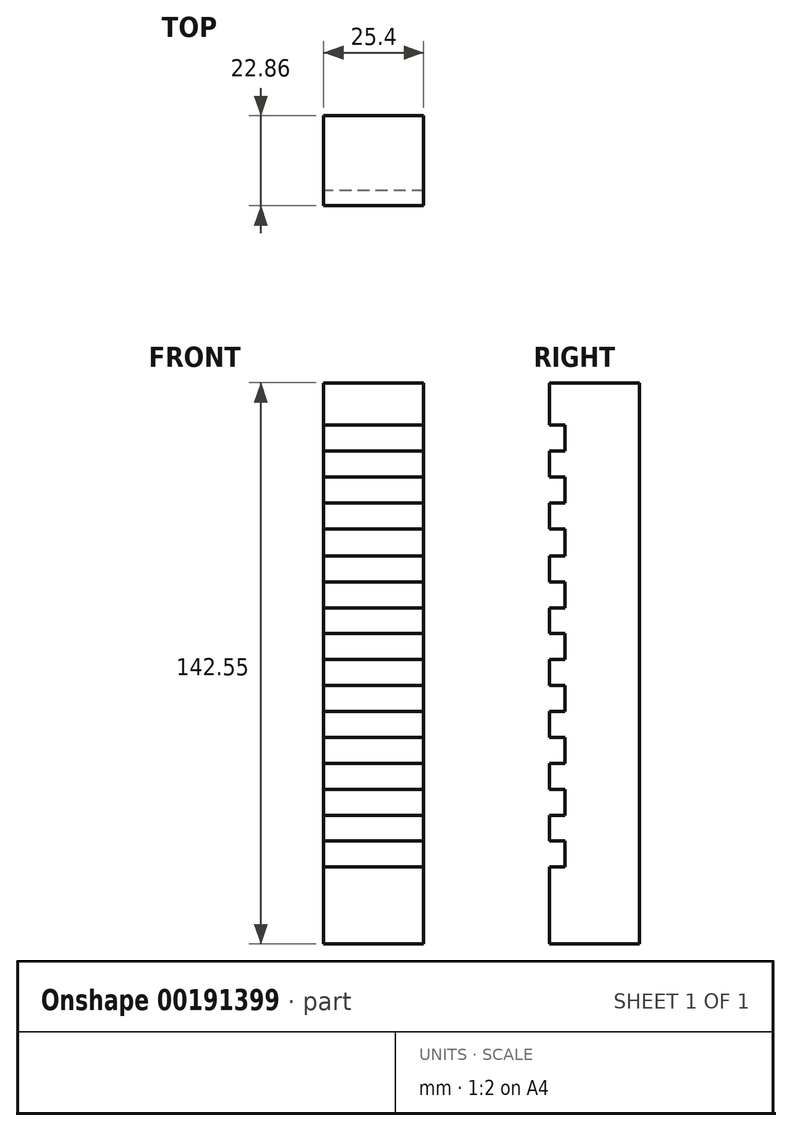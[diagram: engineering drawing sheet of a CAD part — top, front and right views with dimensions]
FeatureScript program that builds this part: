
annotation { "Feature Type Name" : "Feature", "Feature Type Description" : "" }
export const myFeature = defineFeature(function(context is Context, id is Id, definition is map)
    precondition{}
    {
        {
            var Q0;
            Q0=qCreatedBy(makeId("Right.planeOp"),FACE);
            var sketch = newSketch(context, id + "F0", { "sketchPlane" : qUnion([Q0])});
            skLineSegment(sketch, "E0.bottom", {"start": v(17.6, 67.38) * mm, "end": v(40.45, 67.38) * mm});
            skLineSegment(sketch, "E0.top", {"start": v(17.6, -75.17) * mm, "end": v(40.45, -75.17) * mm});
            skLineSegment(sketch, "E0.left", {"start": v(17.6, 67.38) * mm, "end": v(17.6, 56.65) * mm});
            skLineSegment(sketch, "E0.right", {"start": v(40.45, 67.38) * mm, "end": v(40.45, -75.17) * mm});
            skPoint(sketch, "E0.middle", {"position": v(29.02, -3.9) * mm});
            skLineSegment(sketch, "E1", {"start": v(17.6, 56.65) * mm, "end": v(21.46, 56.65) * mm});
            skLineSegment(sketch, "E2", {"start": v(21.46, 56.65) * mm, "end": v(21.46, 50.06) * mm});
            skLineSegment(sketch, "E3", {"start": v(21.46, 50.06) * mm, "end": v(17.6, 50.06) * mm});
            skLineSegment(sketch, "E4", {"start": v(17.6, 50.06) * mm, "end": v(17.6, 43.47) * mm});
            skLineSegment(sketch, "E5", {"start": v(17.6, 43.47) * mm, "end": v(21.46, 43.47) * mm});
            skLineSegment(sketch, "E6", {"start": v(21.46, 43.47) * mm, "end": v(21.46, 36.88) * mm});
            skLineSegment(sketch, "E7", {"start": v(21.46, 36.88) * mm, "end": v(17.6, 36.88) * mm});
            skLineSegment(sketch, "E8", {"start": v(17.6, 36.88) * mm, "end": v(17.6, 30.3) * mm});
            skLineSegment(sketch, "E9", {"start": v(17.6, 30.3) * mm, "end": v(21.46, 30.3) * mm});
            skLineSegment(sketch, "E10", {"start": v(21.46, 30.3) * mm, "end": v(21.46, 23.4) * mm});
            skLineSegment(sketch, "E11", {"start": v(21.46, 23.4) * mm, "end": v(17.6, 23.4) * mm});
            skLineSegment(sketch, "E12", {"start": v(17.6, 23.4) * mm, "end": v(17.6, 16.82) * mm});
            skLineSegment(sketch, "E13", {"start": v(17.6, 16.82) * mm, "end": v(21.46, 16.82) * mm});
            skLineSegment(sketch, "E14", {"start": v(21.46, 16.82) * mm, "end": v(21.46, 10.23) * mm});
            skLineSegment(sketch, "E15", {"start": v(21.46, 10.23) * mm, "end": v(17.6, 10.23) * mm});
            skLineSegment(sketch, "E16", {"start": v(17.6, 10.23) * mm, "end": v(17.6, 3.64) * mm});
            skLineSegment(sketch, "E17", {"start": v(17.6, 3.64) * mm, "end": v(21.46, 3.64) * mm});
            skLineSegment(sketch, "E18", {"start": v(21.46, 3.64) * mm, "end": v(21.46, -2.95) * mm});
            skLineSegment(sketch, "E19", {"start": v(21.46, -2.95) * mm, "end": v(17.6, -2.95) * mm});
            skLineSegment(sketch, "E20", {"start": v(17.6, -2.95) * mm, "end": v(17.6, -9.54) * mm});
            skLineSegment(sketch, "E21", {"start": v(17.6, -9.54) * mm, "end": v(21.46, -9.54) * mm});
            skLineSegment(sketch, "E22", {"start": v(21.46, -9.54) * mm, "end": v(21.46, -16.13) * mm});
            skLineSegment(sketch, "E23", {"start": v(21.46, -16.13) * mm, "end": v(17.6, -16.13) * mm});
            skLineSegment(sketch, "E24", {"start": v(17.6, -16.13) * mm, "end": v(17.6, -22.72) * mm});
            skLineSegment(sketch, "E25", {"start": v(17.6, -22.72) * mm, "end": v(21.46, -22.72) * mm});
            skLineSegment(sketch, "E26", {"start": v(21.46, -22.72) * mm, "end": v(21.46, -29.3) * mm});
            skLineSegment(sketch, "E27", {"start": v(21.46, -29.3) * mm, "end": v(17.6, -29.3) * mm});
            skLineSegment(sketch, "E28", {"start": v(17.6, -29.3) * mm, "end": v(17.6, -35.9) * mm});
            skLineSegment(sketch, "E29", {"start": v(17.6, -35.9) * mm, "end": v(21.46, -35.9) * mm});
            skLineSegment(sketch, "E30", {"start": v(21.46, -35.9) * mm, "end": v(21.46, -42.48) * mm});
            skLineSegment(sketch, "E31", {"start": v(21.46, -42.48) * mm, "end": v(17.6, -42.48) * mm});
            skLineSegment(sketch, "E32", {"start": v(17.6, -42.48) * mm, "end": v(17.6, -49.07) * mm});
            skLineSegment(sketch, "E33", {"start": v(17.6, -49.07) * mm, "end": v(21.46, -49.07) * mm});
            skLineSegment(sketch, "E34", {"start": v(21.46, -49.07) * mm, "end": v(21.46, -55.66) * mm});
            skLineSegment(sketch, "E35", {"start": v(21.46, -55.66) * mm, "end": v(17.6, -55.66) * mm});
            skLineSegment(sketch, "E36", {"start": v(17.6, -55.66) * mm, "end": v(17.6, -75.17) * mm});
            skSolve(sketch);
        }
        {
            var Q0;
            Q0 = qSketchRegion(id + "F0", true);
            extrude(context, id + "F1", {"entities" : qUnion([Q0]), "endBound" : BoundingType.SYMMETRIC, "depth" : 25.4 * mm});
        }
    });
